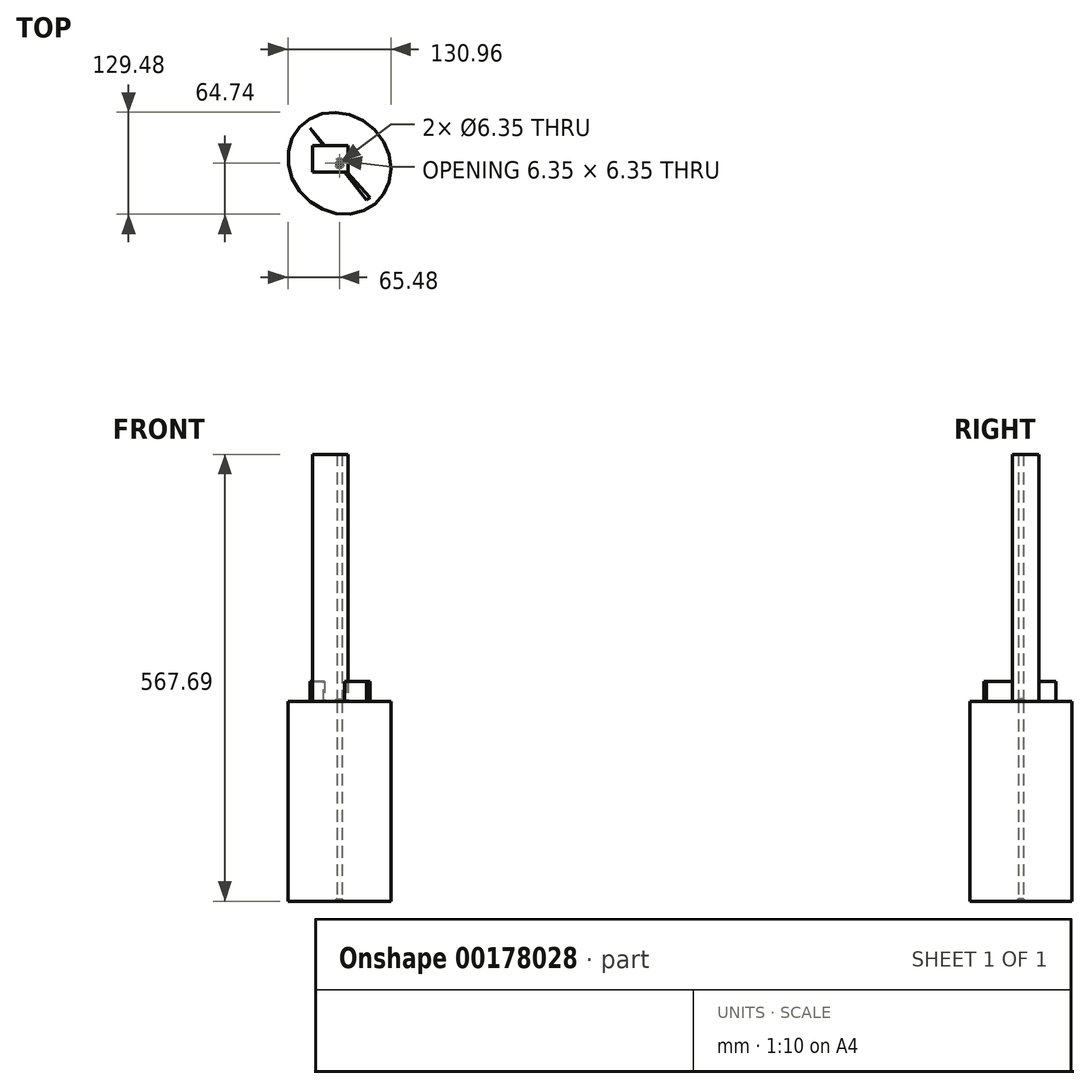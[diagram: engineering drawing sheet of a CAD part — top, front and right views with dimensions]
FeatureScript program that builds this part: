
annotation { "Feature Type Name" : "Feature", "Feature Type Description" : "" }
export const myFeature = defineFeature(function(context is Context, id is Id, definition is map)
    precondition{}
    {
        {
            var Q0;
            Q0=qCreatedBy(makeId("Top.planeOp"),FACE);
            var sketch = newSketch(context, id + "F0", { "sketchPlane" : qUnion([Q0])});
            skLineSegment(sketch, "E0", {"start": v(0, 0) * mm, "end": v(-37.6, 44.71) * mm});
            skLineSegment(sketch, "E1", {"start": v(-37.6, 44.71) * mm, "end": v(34.35, -46.79) * mm});
            skLineSegment(sketch, "E2", {"start": v(34.35, -46.79) * mm, "end": v(38.8, -43.83) * mm});
            skLineSegment(sketch, "E3", {"start": v(38.8, -43.83) * mm, "end": v(-3.54, 4.2) * mm});
            skSolve(sketch);
        }
        {
            var Q0;
            Q0 = qSketchRegion(id + "F0", true);
            extrude(context, id + "F1", {"entities" : qUnion([Q0]), "depth" : 25.4 * mm});
        }
        {
            var Q0;
            Q0=qCreatedBy(makeId("Top.planeOp"),FACE);
            var sketch = newSketch(context, id + "F2", { "sketchPlane" : qUnion([Q0])});
            skLineSegment(sketch, "E4.bottom", {"start": v(-34.42, 22.57) * mm, "end": v(11.17, 22.57) * mm});
            skLineSegment(sketch, "E4.top", {"start": v(-34.42, -11.07) * mm, "end": v(11.17, -11.07) * mm});
            skLineSegment(sketch, "E4.left", {"start": v(-34.42, 22.57) * mm, "end": v(-34.42, -11.07) * mm});
            skLineSegment(sketch, "E4.right", {"start": v(11.17, 22.57) * mm, "end": v(11.17, -11.07) * mm});
            skSolve(sketch);
        }
        {
            var Q0;
            Q0 = qSketchRegion(id + "F2", true);
            extrude(context, id + "F3", {"entities" : qUnion([Q0]), "operationType" : NewBodyOperationType.ADD, "depth" : 313.7 * mm});
        }
        {
            var Q0;
            Q0=makeQuery(id+"F3.boolean.opBoolean","MERGE",FACE,{"derivedFrom":[makeQuery(id+"F1.opExtrude","CAP_FACE",FACE,{"disambiguationData":[OSD([sQuery(id+"F0.wireOp",EDGE,"E0"),sQuery(id+"F0.wireOp",EDGE,"E1"),sQuery(id+"F0.wireOp",EDGE,"E2"),sQuery(id+"F0.wireOp",EDGE,"E3")])],"isStart":true}),makeQuery(id+"F3.opExtrude","CAP_FACE",FACE,{"disambiguationData":[OSD([sQuery(id+"F2.wireOp",EDGE,"E4.bottom"),sQuery(id+"F2.wireOp",EDGE,"E4.top"),sQuery(id+"F2.wireOp",EDGE,"E4.left"),sQuery(id+"F2.wireOp",EDGE,"E4.right")])],"isStart":true})]});
            var sketch = newSketch(context, id + "F4", { "sketchPlane" : qUnion([Q0])});
            skEllipse(sketch, "E5", {"center": v(0, 0) * mm, "majorRadius": 61.53 * mm, "minorRadius": 68.5 * mm, "majorAxis": v(-0.67, 0.74)});
            skSolve(sketch);
        }
        {
            var Q0;
            Q0 = qSketchRegion(id + "F4", true);
            extrude(context, id + "F5", {"entities" : qUnion([Q0]), "operationType" : NewBodyOperationType.ADD, "depth" : 254 * mm});
        }
        {
            var Q0;
            Q0=makeQuery(id+"F5.opExtrude","CAP_FACE",FACE,{"disambiguationData":[OSD([sQuery(id+"F4.wireOp",EDGE,"E5")])],"isStart":false});
            var sketch = newSketch(context, id + "F6", { "sketchPlane" : qUnion([Q0])});
            skCircle(sketch, "E6", {"center": v(0, 0) * mm, "radius": 46.17 * mm});
            skSolve(sketch);
        }
        {
            var Q0;
            Q0=sQuery(id+"F6.wireOp",VERTEX,"E6.center");
            var Q1;
            Q1=makeQuery(id+"F1.opExtrude","SWEPT_BODY",BODY,{"disambiguationData":[OSD([sQuery(id+"F0.wireOp",EDGE,"E0"),sQuery(id+"F0.wireOp",EDGE,"E1"),sQuery(id+"F0.wireOp",EDGE,"E2"),sQuery(id+"F0.wireOp",EDGE,"E3")])]});
            hole(context, id + "F7", {"style" : HoleStyle.C_SINK, "endStyle" : HoleEndStyle.THROUGH, "holeDiameter" : 6.35 * mm, "cSinkDiameter" : 12.7 * mm, "cSinkAngle" : 90 * degree, "locations" : qUnion([Q0]), "scope" : qUnion([Q1]), "isTappedThrough" : true});
        }
        {
            var Q0;
            Q0=sQuery(id+"F4.wireOp",VERTEX,"E5.center");
            var Q1;
            Q1=makeQuery(id+"F1.opExtrude","SWEPT_BODY",BODY,{"disambiguationData":[OSD([sQuery(id+"F0.wireOp",EDGE,"E0"),sQuery(id+"F0.wireOp",EDGE,"E1"),sQuery(id+"F0.wireOp",EDGE,"E2"),sQuery(id+"F0.wireOp",EDGE,"E3")])]});
            hole(context, id + "F8", {"style" : HoleStyle.C_SINK, "endStyle" : HoleEndStyle.THROUGH, "holeDiameter" : 6.35 * mm, "cSinkDiameter" : 12.7 * mm, "cSinkAngle" : 90 * degree, "locations" : qUnion([Q0]), "scope" : qUnion([Q1]), "isTappedThrough" : true});
        }
    });
